# Revit family: 947140001_Grif. Orinal Push Exp 3-4 Racor
name_source: partatom
category: Plumbing Fixtures
units: mm (PartAtom-declared; Revit-internal decimal feet)

## family parameters
Always vertical = Yes
Cut with Voids When Loaded = No
Host = Wall
OmniClass Number = 23.31.11.00
OmniClass Title = Faucets
Part Type = Normal
Room Calculation Point = No
Round Connector Dimension = Use Diameter
Shared = No

## types (1)
- Orinal Push Exp 3/4"
    Alto = 303.8 mm  [stored 0.996719 ft]
    Alto 2 = 272.3 mm  [stored 0.893373 ft]
    Ancho = 129 mm  [stored 0.423228 ft]
    Capacidad de flujo = 6,5 - 9,68 L/min - 0,33 - 0,49 L/Descarga.
    Capacidad de flujo máximo por norma = 9,68 L/min - 0,49 L/Descarga.
    Creado por = BIMBAU
    Cuidado Y Limpieza = Los acabados superficiales son aquellos que le imprimen una apariencia especial y estética a su producto y además le brindan protección. Para prolongar sus cualidades es vital que la limpieza profunda del producto se haga únicamente con agua y jabón suave y que en el secado y el brillo se utilice un paño de algodón limpio, dicha limpieza se recomienda 2 veces a la semana, y en zonas costeras a diario por la salinidad del ambiente. Por ningún motivo deben usarse elementos abrasivos, ácidos o disolventes para la limpieza del producto. Los acabados pueden variar su comportamiento en zonas costeras y/o en ambientes corrosivos.
    Default Elevation = 0 mm  [stored 0 ft]
    Description = Las válvulas para orinal Corona son el aliado perfecto para las necesidades de las instituciones
de alto tráfico, están diseñadas para un óptimo funcionamiento y durabilidad debido a sus
características antivandálicas.
    Diametro 2 = 63 mm  [stored 0.206693 ft]
    Diametro de tuberia = 1/2 NPT.
    Diámetro = 65.1 mm  [stored 0.213583 ft]
    Fecha de creación = 12/04/2021
    Manufacturer = Corona
    Material = Corona_Cromado
    Model = Orinal Push
    Normatividad = NTC 1644
    Peso Bruto aprox = 560g 1,23lb.
    Peso Neto aprox = 500g 1,10lb.
    Presion maxima = 80 Psi.
    Presion minima = 20 Psi.
    Rango presion de agua = Entre 20 y 80 Psi
    Recubrimientos = -Resistente a la corrosión, pelado y decoloración por agua. -Producto para uso institucional.
    Referencia = 947140001
    Type Comments = -GriferÍa para orinal tipo push metálica.-Consumo de agua desde 0.5 L hasta 1.9 L. -Cierre automático temporizado entre 3 a 9 segundos.
    URL = https://corona.co
    Vida útil = 150 Mil Ciclos

note: [stored X ft] marks values corroborated as IEEE doubles in the binary element streams (Revit-internal decimal feet)

## geometry (parser evidence)
native form markers: Sweep x2
no freeform markers — native parametric forms only
